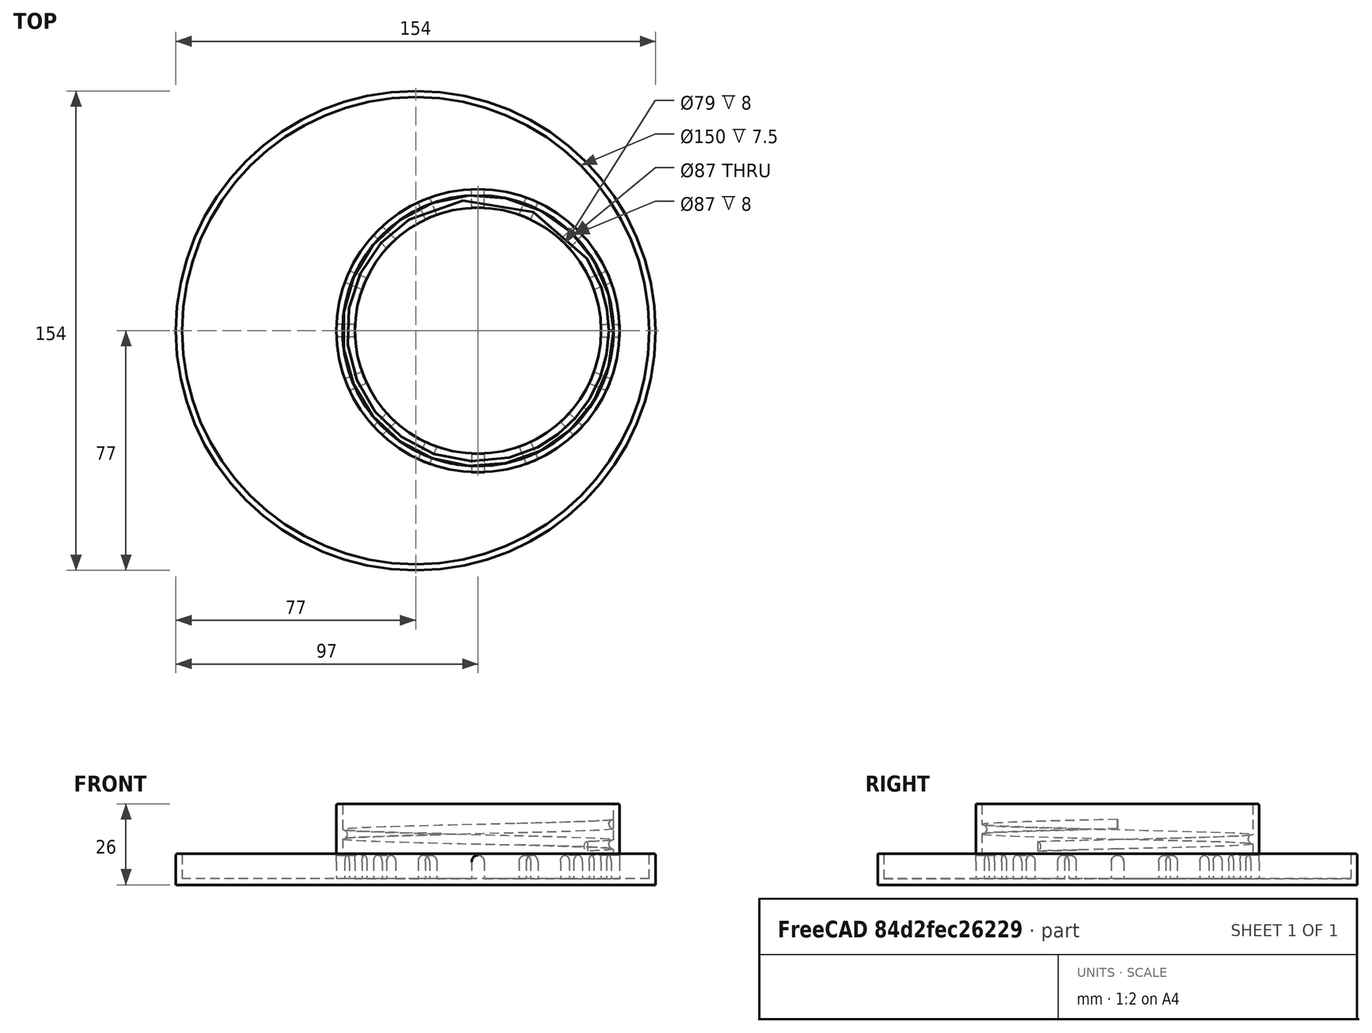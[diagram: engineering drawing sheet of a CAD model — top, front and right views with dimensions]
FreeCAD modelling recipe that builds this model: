
FCSTD DOCUMENT  (FreeCAD 2023.131R26244 +5365 (Git))
Label: Mason Jar Water Dispensor
License: All rights reserved
LicenseURL: http://en.wikipedia.org/wiki/All_rights_reserved
objects: Sketcher::SketchObject×6, PartDesign::Pad×4, Spreadsheet::Sheet×1, PartDesign::Body×1, PartDesign::Pocket×1, PartDesign::PolarPattern×1, PartDesign::AdditiveHelix×1, PartDesign::Fillet×1
note: 37 computed .brp shape members not serialized (recipe doc carries the construction recipe); baked Part::Feature solids carry a one-line shape summary decoded from their .brp

FEATURE [Spreadsheet::Sheet] Spreadsheet  label="Parameters"
  PythonMode = false
  ShowCells = 0
  TreeRank = 1
  cells = A2=Ring Inner Diameter; B2(Ring_Inner_Diameter)=87; C2=Should be large enough to fit over the threads on the glass jar.; A3=Ring Side Height; B3(Ring_Side_Height)=16; C3=How much material will screw onto the jar.; A5=Bowl Inner Diameter; B5(Bowl_Inner_Diameter)=150; C5=The size of the bowl that will hold the water.; A6=Bowl Wall Height; B6(Bowl_Wall_Height)=8; C6=The height of the sides of the bowl.; A7=Bowl Offset; B7(Bowl_Offset)=20; C7=Use this to position the mason jar off-center in the bigger bowl. This allows more space for your pet to drink.; A9=Thread Pitch; B9(Thread_Pitch)=6.5; C9=The thread pitch.; A10=Thread Width; B10(Thread_Width)=3; C10=The distance between two thread on the jar.; A11=Thread Height; B11(Thread_Height)=3; C11=The height of the threads from the inner survace of the lid.; A12=Thread Offset; B12(Thread_Offset)=2; C12=Distance from the bottom of the ring where the threads start.; A13=Thread Turns; B13(Thread_Turns)=1.1; C13=The number of turns inside the ring.; A15=Wall Thickness; B15(Wall_Thickness)=2; C15=The thickness of all walls in the model. 1.00mm should be the minimum.
FEATURE [Sketcher::SketchObject] Sketch  label="Mason Jar Ring Sketch"
  ArcFitTolerance = 1e-06
  AttachmentSupport = -> [XY_Plane]
  ExternalBSplineMaxDegree = 5
  ExternalBSplineTolerance = 0.0001
  FullyConstrained = true
  InternalTolerance = 1e-06
  InvalidShape = false
  MakeInternals = false
  MapMode = 5
  Support = -> [XY_Plane]
  TreeRank = 12
  ValidateShape = true
  expr: Constraints[1] = <<Parameters>>.Ring_Inner_Diameter + 2 * <<Parameters>>.Wall_Thickness
  expr: Constraints[3] = <<Parameters>>.Ring_Inner_Diameter
  sketch-geometry (2):
    g0: Circle CenterX=0 CenterY=0 CenterZ=0 NormalX=0 NormalY=0 NormalZ=1 AngleXU=0 Radius=45.5
    g1: Circle CenterX=0 CenterY=0 CenterZ=0 NormalX=0 NormalY=0 NormalZ=1 AngleXU=0 Radius=43.5
  constraints (4):
    c: Coincident(g0,g-1)
    c: Diameter(g0) = 91
    c: Coincident(g1,g0)
    c: Diameter(g1) = 87
FEATURE [PartDesign::Pad] Pad  label="Mason Jar Ring"
  AddSubType = 0
  AlongSketchNormal = false
  AutoTaperInnerAngle = true
  CheckUpToFaceLimits = true
  ClaimChildren = false
  Direction = (0,0,1)
  Fit = 0
  FitJoin = 0
  InnerFit = 0
  InnerFitJoin = 0
  InvalidShape = false
  Length = 24
  Length2 = 100
  Linearize = true
  NewSolid = false
  Profile = -> Sketch
  Suppress = false
  TaperInnerAngle = 0
  TaperInnerAngleRev = 0
  TreeRank = 13
  Type = 0
  ValidateShape = true
  _ProfileBasedVersion = 1
  expr: Length = <<Parameters>>.Ring_Side_Height + <<Parameters>>.Bowl_Wall_Height
FEATURE [Sketcher::SketchObject] Sketch001  label="Water Outlet Profile"
  ArcFitTolerance = 1e-06
  AttachmentSupport = -> [XZ_Plane]
  ExternalBSplineMaxDegree = 5
  ExternalBSplineTolerance = 0.0001
  FullyConstrained = true
  InternalTolerance = 1e-06
  InvalidShape = false
  MakeInternals = false
  MapMode = 5
  Placement = pos=(0,0,0) rot=(1,0,0;1.5708rad)
  Support = -> [XZ_Plane]
  TreeRank = 14
  ValidateShape = true
  expr: Constraints[11] = <<Parameters>>.Bowl_Wall_Height - 2.5
  sketch-geometry (5):
    g0: LineSegment StartX=-2 StartY=0 StartZ=0 EndX=-2 EndY=5.5 EndZ=0
    g1: LineSegment StartX=2 StartY=0 StartZ=0 EndX=2 EndY=5.5 EndZ=0
    g2: ArcOfCircle CenterX=1e-16 CenterY=5.5 CenterZ=0 NormalX=0 NormalY=0 NormalZ=1 AngleXU=0 Radius=2 StartAngle=9e-16 EndAngle=3.14159
    g3: LineSegment StartX=-2 StartY=0 StartZ=0 EndX=2 EndY=0 EndZ=0
    g4: LineSegment [constr] StartX=-2 StartY=5.5 StartZ=0 EndX=2 EndY=5.5 EndZ=0
  constraints (15):
    c: PointOnObject(g0,g-1)
    c: Vertical(g0)
    c: PointOnObject(g1,g-1)
    c: Vertical(g1)
    c: Equal(g0,g1)
    c: Coincident(g2,g0)
    c: Coincident(g2,g1)
    c: Radius(g2) = 2
    c: DistanceX(g-1,g1) = 2
    c: Coincident(g3,g0)
    c: Coincident(g3,g1)
    c: Distance(g1,g1) = 5.5
    c: Coincident(g4,g0)
    c: Coincident(g4,g1)
    c: PointOnObject(g2,g4)
FEATURE [Sketcher::SketchObject] Sketch002  label="Thread Profile"
  ArcFitTolerance = 1e-06
  AttachmentSupport = -> [XZ_Plane]
  ExternalBSplineMaxDegree = 5
  ExternalBSplineTolerance = 0.0001
  FullyConstrained = true
  InternalTolerance = 1e-06
  InvalidShape = false
  MakeInternals = false
  MapMode = 5
  Placement = pos=(0,0,0) rot=(1,0,0;1.5708rad)
  Support = -> [XZ_Plane]
  TreeRank = 17
  ValidateShape = true
  expr: Constraints[1] = <<Parameters>>.Thread_Width
  expr: Constraints[5] = <<Parameters>>.Ring_Side_Height + 5 - <<Parameters>>.Thread_Offset
  expr: Constraints[6] = <<Parameters>>.Ring_Inner_Diameter / 2 + 0.01
  sketch-geometry (2):
    g0: LineSegment StartX=43.51 StartY=16 StartZ=0 EndX=43.51 EndY=19 EndZ=0
    g1: ArcOfCircle CenterX=43.51 CenterY=17.5 CenterZ=0 NormalX=0 NormalY=0 NormalZ=1 AngleXU=0 Radius=1.5 StartAngle=1.5708 EndAngle=4.71239
  constraints (7):
    c: Vertical(g0)
    c: Distance(g0,g0) = 3
    c: Coincident(g1,g0)
    c: Coincident(g1,g0)
    c: PointOnObject(g1,g0)
    c: DistanceY(g-1,g0) = 19
    c: DistanceX(g-1,g0) = 43.51
FEATURE [PartDesign::Body] Body
  AutoGroupSolids = false
  ClaimAllChildren = false
  ExportMode = 0
  Group = -> [Sketch,Pad,Sketch001,Pad003,Pocket,PolarPattern,Sketch002,Helix,Sketch003,Pad001,Sketch004,Pad002,Fillet,Sketch005]
  InvalidShape = false
  Origin = -> Origin
  Tip = -> Fillet
  TreeRank = 11
  ValidateShape = true
  _ExportChildren = -> [Pad,Pad003,Pocket,PolarPattern,Helix,Pad001,Pad002,Fillet]
  _GroupVersion = 1
FEATURE [PartDesign::Pocket] Pocket  label="Water Outlet"
  AddSubType = 1
  AutoTaperInnerAngle = true
  BaseFeature = -> Pad003
  CheckUpToFaceLimits = true
  ClaimChildren = false
  Fit = 0
  FitJoin = 0
  InnerFit = 0
  InnerFitJoin = 0
  InvalidShape = false
  Length = 5
  Length2 = 100
  Linearize = true
  NewSolid = false
  Profile = -> Sketch001
  Suppress = false
  TaperInnerAngle = 0
  TaperInnerAngleRev = 0
  TreeRank = 15
  Type = 1
  ValidateShape = true
  _ProfileBasedVersion = 1
  _Version = 1
FEATURE [PartDesign::PolarPattern] PolarPattern
  AddSubType = 0
  Angle = 360
  Axis = -> Z_Axis
  BaseFeature = -> Pocket
  CopyShape = false
  InvalidShape = false
  NewSolid = false
  Occurrences = 16
  OriginalSubs = -> [Pocket]
  Originals = -> [Pocket]
  ParallelTransform = true
  SubTransform = true
  Suppress = false
  TreeRank = 16
  ValidateShape = true
  _Version = 3
FEATURE [PartDesign::AdditiveHelix] Helix  label="Threads"
  AddSubType = 0
  Angle = 0
  Axis = (0,0,1)
  Base = (0,0,0)
  BaseFeature = -> PolarPattern
  ClaimChildren = false
  Fit = 0
  FitJoin = 0
  Growth = 0
  HasBeenEdited = true
  Height = 7.15
  InnerFit = 0
  InnerFitJoin = 0
  InvalidShape = false
  LeftHanded = false
  Linearize = true
  Mode = 1
  NewSolid = false
  Outside = false
  Pitch = 6.5
  Profile = -> Sketch002
  ReferenceAxis = -> Sketch002 [V_Axis]
  Reversed = true
  Suppress = false
  TreeRank = 18
  Turns = 1.1
  ValidateShape = true
  _ProfileBasedVersion = 1
  expr: Pitch = <<Parameters>>.Thread_Pitch
  expr: Turns = <<Parameters>>.Thread_Turns
FEATURE [Sketcher::SketchObject] Sketch003  label="Bowl Base Sketch"
  ArcFitTolerance = 1e-06
  AttachmentSupport = -> [Helix]
  ExternalBSplineMaxDegree = 5
  ExternalBSplineTolerance = 0.0001
  FullyConstrained = true
  InternalTolerance = 1e-06
  InvalidShape = false
  MakeInternals = false
  MapMode = 5
  Placement = pos=(0,0,0) rot=(1,0,0;3.14159rad)
  Support = -> [Helix]
  TreeRank = 19
  ValidateShape = true
  expr: Constraints[1] = <<Parameters>>.Bowl_Offset
  expr: Constraints[2] = <<Parameters>>.Bowl_Inner_Diameter + 2 * <<Parameters>>.Wall_Thickness
  sketch-geometry (1):
    g0: Circle CenterX=-20 CenterY=0 CenterZ=0 NormalX=0 NormalY=0 NormalZ=1 AngleXU=0 Radius=77
  constraints (3):
    c: PointOnObject(g0,g-1)
    c: DistanceX(g0,g-1) = 20
    c: Diameter(g0) = 154
FEATURE [PartDesign::Pad] Pad001  label="Bowl Base"
  AddSubType = 0
  AlongSketchNormal = false
  AutoTaperInnerAngle = true
  BaseFeature = -> Helix
  CheckUpToFaceLimits = true
  ClaimChildren = false
  Direction = (0,0,-1)
  Fit = 0
  FitJoin = 0
  InnerFit = 0
  InnerFitJoin = 0
  InvalidShape = false
  Length = 2
  Length2 = 100
  Linearize = true
  NewSolid = false
  Profile = -> Sketch003
  Suppress = false
  TaperInnerAngle = 0
  TaperInnerAngleRev = 0
  TreeRank = 20
  Type = 0
  ValidateShape = true
  _ProfileBasedVersion = 1
  expr: Length = <<Parameters>>.Wall_Thickness
FEATURE [Sketcher::SketchObject] Sketch004  label="Bowl Wall Sketch"
  ArcFitTolerance = 1e-06
  AttachmentSupport = -> [Pad001]
  ExternalBSplineMaxDegree = 5
  ExternalBSplineTolerance = 0.0001
  FullyConstrained = true
  InternalTolerance = 1e-06
  InvalidShape = false
  MakeInternals = false
  MapMode = 5
  Support = -> [Pad001]
  TreeRank = 21
  ValidateShape = true
  expr: Constraints[2] = <<Parameters>>.Bowl_Offset
  expr: Constraints[3] = <<Parameters>>.Bowl_Inner_Diameter
  expr: Constraints[4] = <<Parameters>>.Bowl_Inner_Diameter + 2 * <<Parameters>>.Wall_Thickness
  sketch-geometry (2):
    g0: Circle CenterX=-20 CenterY=0 CenterZ=0 NormalX=0 NormalY=0 NormalZ=1 AngleXU=0 Radius=77
    g1: Circle CenterX=-20 CenterY=0 CenterZ=0 NormalX=0 NormalY=0 NormalZ=1 AngleXU=0 Radius=75
  constraints (5):
    c: PointOnObject(g0,g-1)
    c: Coincident(g1,g0)
    c: DistanceX(g0,g-1) = 20
    c: Diameter(g1) = 150
    c: Diameter(g0) = 154
FEATURE [PartDesign::Pad] Pad002  label="Bowl Walls"
  AddSubType = 0
  AlongSketchNormal = false
  AutoTaperInnerAngle = true
  BaseFeature = -> Pad001
  CheckUpToFaceLimits = true
  ClaimChildren = false
  Direction = (0,0,1)
  Fit = 0
  FitJoin = 0
  InnerFit = 0
  InnerFitJoin = 0
  InvalidShape = false
  Length = 8
  Length2 = 100
  Linearize = true
  NewSolid = false
  Profile = -> Sketch004
  Suppress = false
  TaperInnerAngle = 0
  TaperInnerAngleRev = 0
  TreeRank = 22
  Type = 0
  ValidateShape = true
  _ProfileBasedVersion = 1
  expr: Length = <<Parameters>>.Bowl_Wall_Height
FEATURE [PartDesign::Fillet] Fillet
  AddSubType = 0
  Base = -> Pad002 [Face55,Face50]
  BaseFeature = -> Pad002
  InvalidShape = false
  NewSolid = false
  Radius = 0.5
  SupportTransform = false
  Suppress = false
  TreeRank = 23
  ValidateShape = true
FEATURE [Sketcher::SketchObject] Sketch005
  ArcFitTolerance = 1e-06
  AttachmentSupport = -> [Fillet]
  ExternalBSplineMaxDegree = 5
  ExternalBSplineTolerance = 0.0001
  FullyConstrained = true
  InternalTolerance = 1e-06
  InvalidShape = false
  MakeInternals = false
  MapMode = 5
  Support = -> [Fillet]
  TreeRank = 24
  ValidateShape = true
  expr: Constraints[1] = <<Parameters>>.Ring_Inner_Diameter
  expr: Constraints[3] = <<Parameters>>.Ring_Inner_Diameter - 8
  sketch-geometry (2):
    g0: Circle CenterX=0 CenterY=0 CenterZ=0 NormalX=0 NormalY=0 NormalZ=1 AngleXU=0 Radius=43.5
    g1: Circle CenterX=0 CenterY=0 CenterZ=0 NormalX=0 NormalY=0 NormalZ=1 AngleXU=0 Radius=39.5
  constraints (4):
    c: Coincident(g0,g-1)
    c: Diameter(g0) = 87
    c: Coincident(g1,g0)
    c: Diameter(g1) = 79
FEATURE [PartDesign::Pad] Pad003  label="Inner Ring Wall"
  AddSubType = 0
  AlongSketchNormal = false
  AutoTaperInnerAngle = true
  BaseFeature = -> Pad
  CheckUpToFaceLimits = true
  ClaimChildren = false
  Direction = (0,0,1)
  Fit = 0
  FitJoin = 0
  InnerFit = 0
  InnerFitJoin = 0
  InvalidShape = false
  Length = 8
  Length2 = 100
  Linearize = true
  NewSolid = false
  Profile = -> Sketch005
  Suppress = false
  TaperInnerAngle = 0
  TaperInnerAngleRev = 0
  TreeRank = 25
  Type = 0
  ValidateShape = true
  _ProfileBasedVersion = 1
  expr: Length = <<Parameters>>.Bowl_Wall_Height
